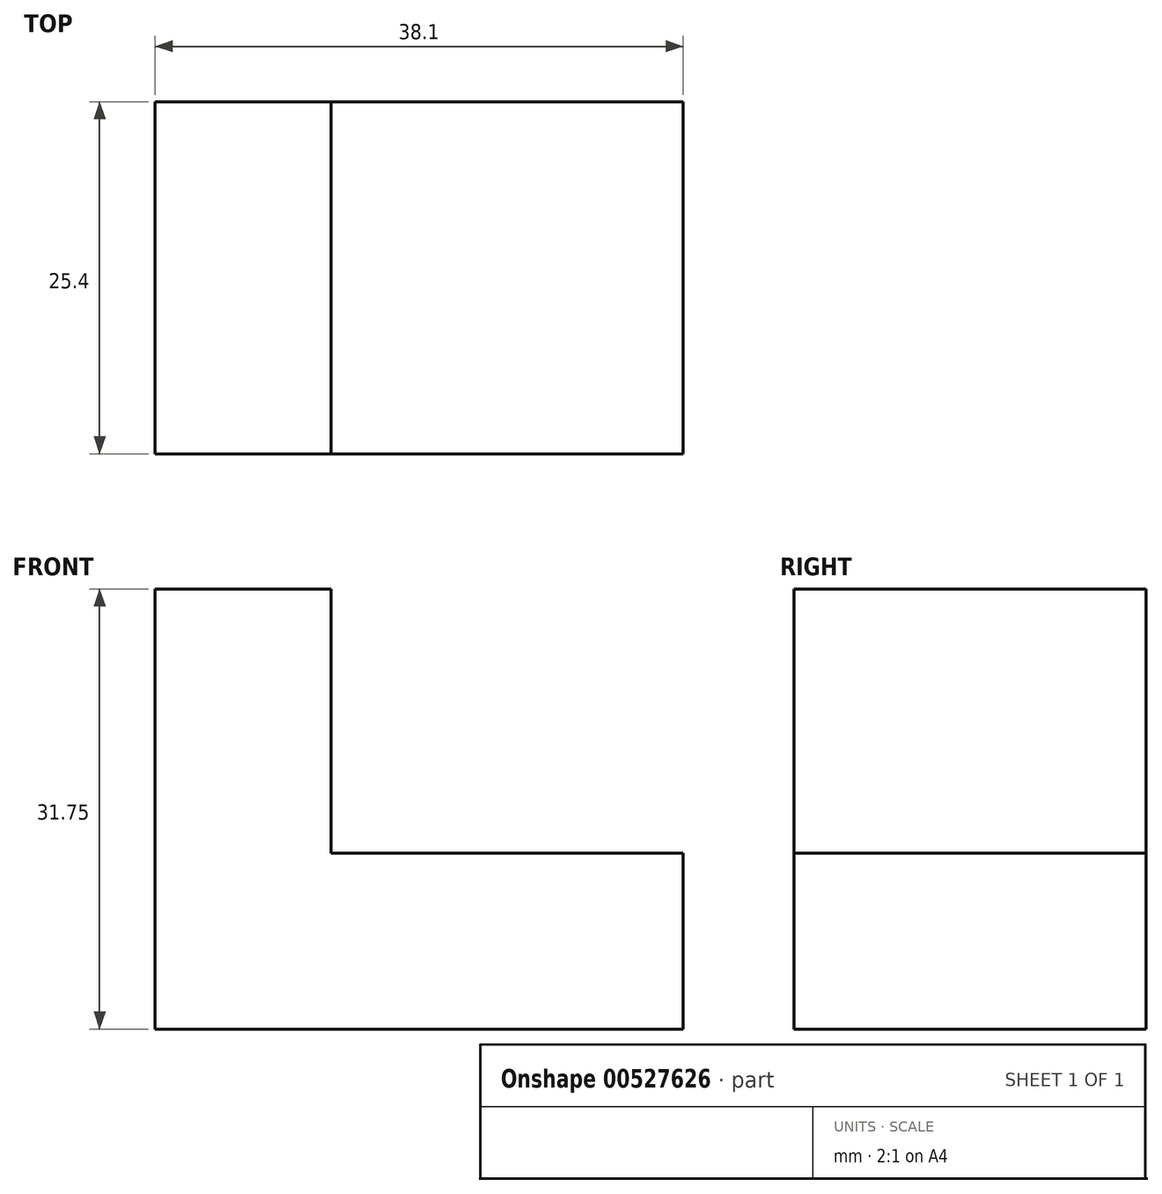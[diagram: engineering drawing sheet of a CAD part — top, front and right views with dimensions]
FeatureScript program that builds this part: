
annotation { "Feature Type Name" : "Feature", "Feature Type Description" : "" }
export const myFeature = defineFeature(function(context is Context, id is Id, definition is map)
    precondition{}
    {
        {
            var Q0;
            Q0=qCreatedBy(makeId("Front.planeOp"),FACE);
            var sketch = newSketch(context, id + "F0", { "sketchPlane" : qUnion([Q0])});
            skLineSegment(sketch, "E0", {"start": v(0, 0) * mm, "end": v(38.1, 0) * mm});
            skLineSegment(sketch, "E1", {"start": v(38.1, 12.7) * mm, "end": v(38.1, 0) * mm});
            skLineSegment(sketch, "E2", {"start": v(0, 31.75) * mm, "end": v(0, 0) * mm});
            skLineSegment(sketch, "E3", {"start": v(0, 31.75) * mm, "end": v(12.7, 31.75) * mm});
            skLineSegment(sketch, "E4", {"start": v(38.1, 12.7) * mm, "end": v(12.7, 12.7) * mm});
            skLineSegment(sketch, "E5", {"start": v(12.7, 31.75) * mm, "end": v(12.7, 12.7) * mm});
            skSolve(sketch);
        }
        {
            var Q0;
            Q0 = qSketchRegion(id + "F0", true);
            extrude(context, id + "F1", {"entities" : qUnion([Q0]), "depth" : 25.4 * mm, "offsetDistance" : 25.4 * mm});
        }
    });
